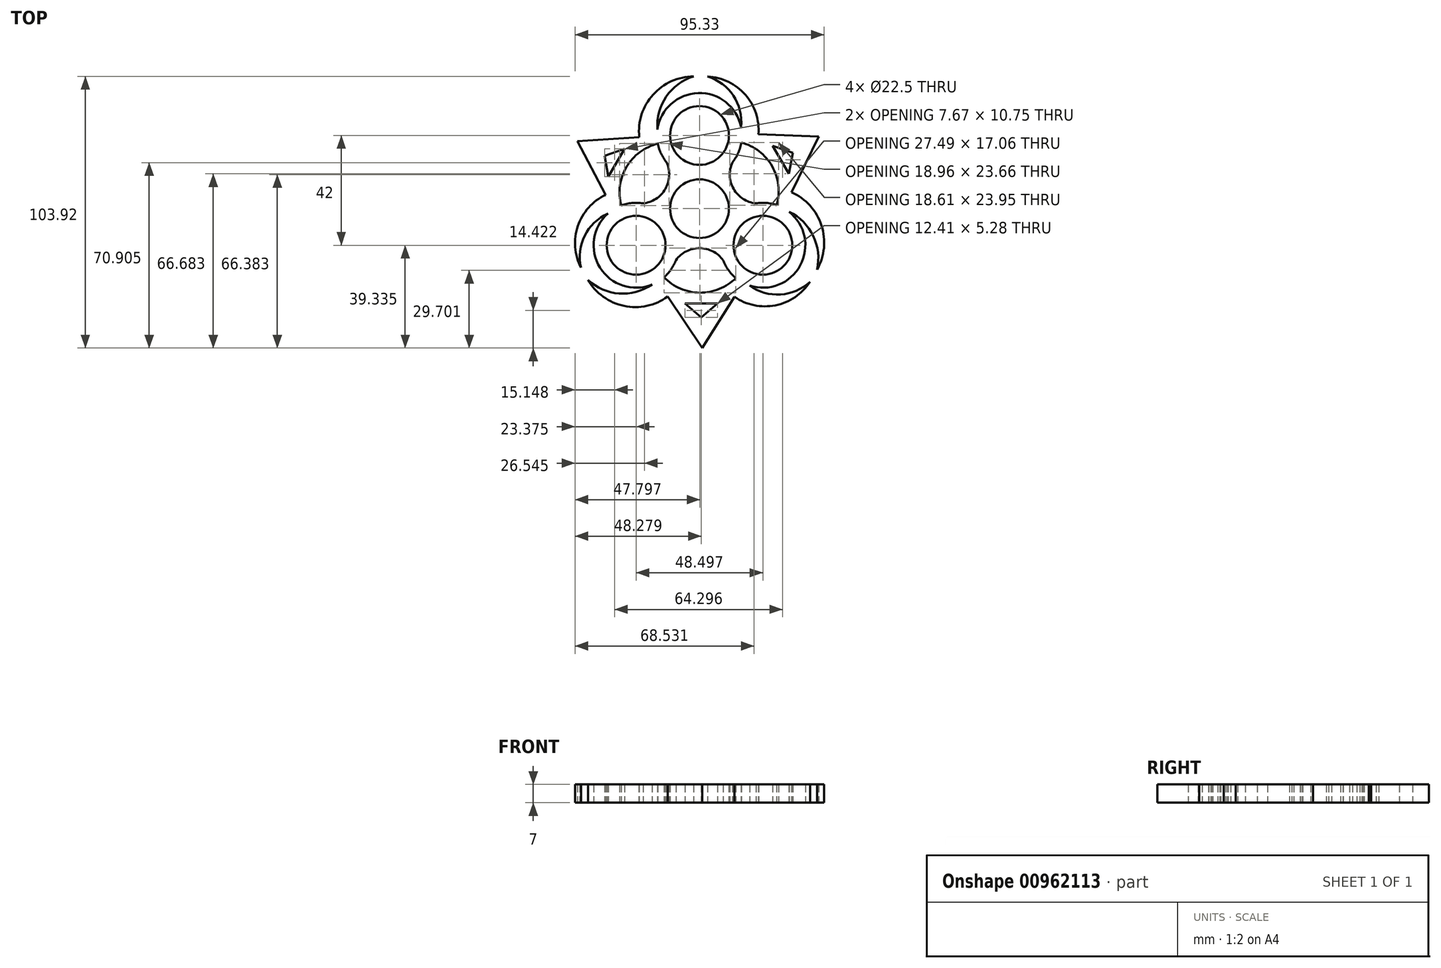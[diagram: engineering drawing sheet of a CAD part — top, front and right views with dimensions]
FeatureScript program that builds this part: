
annotation { "Feature Type Name" : "Feature", "Feature Type Description" : "" }
export const myFeature = defineFeature(function(context is Context, id is Id, definition is map)
    precondition{}
    {
        {
            var Q0;
            Q0=qCreatedBy(makeId("Top.planeOp"),FACE);
            var sketch = newSketch(context, id + "F0", { "sketchPlane" : qUnion([Q0])});
            skCircle(sketch, "E0", {"center": v(-80.13, 35.93) * mm, "radius": 11.25 * mm});
            skCircle(sketch, "E1", {"center": v(-80.13, 63.93) * mm, "radius": 11.25 * mm});
            skCircle(sketch, "E2.1.0", {"center": v(-104.38, 21.93) * mm, "radius": 11.25 * mm});
            skCircle(sketch, "E2.2.0", {"center": v(-55.88, 21.93) * mm, "radius": 11.25 * mm});
            skCircle(sketch, "E3.0", {"center": v(-80.13, 63.93) * mm, "radius": 16.25 * mm});
            skCircle(sketch, "E4.0", {"center": v(-104.38, 21.93) * mm, "radius": 16.25 * mm});
            skCircle(sketch, "E5.0", {"center": v(-55.88, 21.93) * mm, "radius": 16.25 * mm});
            skArc(sketch, "E6", {"start": v(-101.74, 37.97) * mm, "mid": v(-93.21, 43.47) * mm, "end": v(-92.68, 53.61) * mm});
            skArc(sketch, "E7.1.0", {"start": v(-71.08, 16.2) * mm, "mid": v(-80.11, 20.83) * mm, "end": v(-89.16, 16.23) * mm});
            skArc(sketch, "E7.2.0", {"start": v(-67.55, 53.64) * mm, "mid": v(-67.05, 43.5) * mm, "end": v(-58.54, 37.96) * mm});
            skLineSegment(sketch, "E8", {"start": v(-80.13, 63.93) * mm, "end": v(-80.13, 80.18) * mm});
            skLineSegment(sketch, "E9.1.0", {"start": v(-104.38, 21.93) * mm, "end": v(-118.45, 13.8) * mm});
            skLineSegment(sketch, "E9.2.0", {"start": v(-55.88, 21.93) * mm, "end": v(-41.8, 13.8) * mm});
            skArc(sketch, "E10", {"start": v(-96.07, 60.81) * mm, "mid": v(-108.04, 51.92) * mm, "end": v(-110.07, 37.15) * mm});
            skArc(sketch, "E11.1.0", {"start": v(-93.7, 9.68) * mm, "mid": v(-80.01, 3.77) * mm, "end": v(-66.2, 9.4) * mm});
            skArc(sketch, "E11.2.0", {"start": v(-50.6, 37.3) * mm, "mid": v(-52.33, 52.11) * mm, "end": v(-64.1, 61.26) * mm});
            skArc(sketch, "E12", {"start": v(-96.21, 66.22) * mm, "mid": v(-112.39, 54.09) * mm, "end": v(-115.19, 34.07) * mm});
            skArc(sketch, "E13.1.0", {"start": v(-98.31, 6.86) * mm, "mid": v(-79.72, -1.08) * mm, "end": v(-60.98, 6.5) * mm});
            skArc(sketch, "E13.2.0", {"start": v(-45.85, 34.72) * mm, "mid": v(-48.27, 54.8) * mm, "end": v(-64.21, 67.23) * mm});
            skLineSegment(sketch, "E14", {"start": v(-92.33, 2.27) * mm, "end": v(-79.1, -17.4) * mm});
            skPoint(sketch, "E14.endSnap0", {"position": v(-79.1, 2.9) * mm});
            skLineSegment(sketch, "E15", {"start": v(-79.1, -17.4) * mm, "end": v(-66.76, 2.19) * mm});
            skLineSegment(sketch, "E16.1.0", {"start": v(-34.45, 63.5) * mm, "end": v(-57.58, 64.38) * mm});
            skLineSegment(sketch, "E16.1.1", {"start": v(-44.87, 42.2) * mm, "end": v(-34.45, 63.5) * mm});
            skLineSegment(sketch, "E16.2.0", {"start": v(-126.83, 61.7) * mm, "end": v(-116.03, 41.23) * mm});
            skLineSegment(sketch, "E16.2.1", {"start": v(-103.18, 63.33) * mm, "end": v(-126.83, 61.7) * mm});
            skLineSegment(sketch, "E17", {"start": v(-85.68, -0.34) * mm, "end": v(-73.27, -0.34) * mm});
            skLineSegment(sketch, "E18", {"start": v(-73.27, -0.34) * mm, "end": v(-79.47, -5.62) * mm});
            skPoint(sketch, "E18.endSnap0", {"position": v(-79.47, -0.34) * mm});
            skLineSegment(sketch, "E19", {"start": v(-79.47, -5.62) * mm, "end": v(-85.68, -0.34) * mm});
            skPoint(sketch, "E20.center", {"position": v(3.03, 6.5) * mm});
            skLineSegment(sketch, "E21.1.0", {"start": v(-52.14, 60.01) * mm, "end": v(-44.47, 57.28) * mm});
            skLineSegment(sketch, "E21.1.1", {"start": v(-44.47, 57.28) * mm, "end": v(-45.94, 49.27) * mm});
            skLineSegment(sketch, "E21.1.2", {"start": v(-45.94, 49.27) * mm, "end": v(-52.14, 60.01) * mm});
            skLineSegment(sketch, "E21.2.0", {"start": v(-114.97, 48.13) * mm, "end": v(-116.44, 56.14) * mm});
            skLineSegment(sketch, "E21.2.1", {"start": v(-116.44, 56.14) * mm, "end": v(-108.77, 58.88) * mm});
            skLineSegment(sketch, "E21.2.2", {"start": v(-108.77, 58.88) * mm, "end": v(-114.97, 48.13) * mm});
            skArc(sketch, "E22", {"start": v(-82.36, 86.52) * mm, "mid": v(-97.92, 79.55) * mm, "end": v(-103.18, 63.33) * mm});
            skArc(sketch, "E23", {"start": v(-82.36, 86.52) * mm, "mid": v(-92.87, 78.81) * mm, "end": v(-96.21, 66.22) * mm});
            skArc(sketch, "E24", {"start": v(-57.58, 64.38) * mm, "mid": v(-62.61, 79.57) * mm, "end": v(-77.02, 86.52) * mm});
            skArc(sketch, "E25", {"start": v(-64.21, 67.23) * mm, "mid": v(-67.17, 79.17) * mm, "end": v(-77.02, 86.52) * mm});
            skArc(sketch, "E26.1.0", {"start": v(-122.82, 8.7) * mm, "mid": v(-110.9, 3.46) * mm, "end": v(-98.31, 6.86) * mm});
            skArc(sketch, "E26.1.1", {"start": v(-122.82, 8.7) * mm, "mid": v(-109, -1.28) * mm, "end": v(-92.33, 2.27) * mm});
            skArc(sketch, "E26.1.2", {"start": v(-115.19, 34.07) * mm, "mid": v(-124.05, 25.54) * mm, "end": v(-125.5, 13.33) * mm});
            skArc(sketch, "E26.1.3", {"start": v(-116.03, 41.23) * mm, "mid": v(-126.67, 29.29) * mm, "end": v(-125.5, 13.33) * mm});
            skArc(sketch, "E26.2.0", {"start": v(-35.2, 12.58) * mm, "mid": v(-36.62, 25.53) * mm, "end": v(-45.85, 34.72) * mm});
            skArc(sketch, "E26.2.1", {"start": v(-35.2, 12.58) * mm, "mid": v(-33.46, 29.54) * mm, "end": v(-44.87, 42.2) * mm});
            skArc(sketch, "E26.2.2", {"start": v(-60.98, 6.5) * mm, "mid": v(-49.17, 3.1) * mm, "end": v(-37.87, 7.95) * mm});
            skArc(sketch, "E26.2.3", {"start": v(-66.76, 2.19) * mm, "mid": v(-51.1, -1.05) * mm, "end": v(-37.87, 7.95) * mm});
            skSolve(sketch);
        }
        {
            var Q0;
            Q0=makeQuery(id+"F0.imprint","IMPRINT",FACE,{"disambiguationData":[TD([[makeQuery(id+"F0.imprint","IMPRINT",EDGE,{"derivedFrom":sQuery(id+"F0.wireOp",EDGE,"E2.1.0")}),-1.0]])]});
            var Q1;
            Q1=makeQuery(id+"F0.imprint","IMPRINT",FACE,{"disambiguationData":[TD([[makeQuery(id+"F0.imprint","IMPRINT",EDGE,{"derivedFrom":sQuery(id+"F0.wireOp",EDGE,"E0")}),-1.0]])]});
            var Q2;
            Q2=makeQuery(id+"F0.imprint","IMPRINT",FACE,{"disambiguationData":[TD([[makeQuery(id+"F0.imprint","IMPRINT",EDGE,{"derivedFrom":sQuery(id+"F0.wireOp",EDGE,"E2.2.0")}),-1.0]])]});
            var Q3;
            Q3=makeQuery(id+"F0.imprint","IMPRINT",FACE,{"disambiguationData":[TD([[makeQuery(id+"F0.imprint","IMPRINT",EDGE,{"derivedFrom":sQuery(id+"F0.wireOp",EDGE,"E1")}),-1.0]])]});
            var Q4;
            {var subQ0=sQuery(id+"F0.wireOp",EDGE,"E10");Q4=makeQuery(id+"F0.imprint","IMPRINT",FACE,{"disambiguationData":[TD([[makeQuery(id+"F0.imprint","IMPRINT",EDGE,{"derivedFrom":subQ0}),-1.0]])]});}
            var Q5;
            {var subQ0=sQuery(id+"F0.wireOp",EDGE,"E11.1.0");Q5=makeQuery(id+"F0.imprint","IMPRINT",FACE,{"disambiguationData":[TD([[makeQuery(id+"F0.imprint","IMPRINT",EDGE,{"derivedFrom":subQ0}),-1.0]])]});}
            var Q6;
            {var subQ0=sQuery(id+"F0.wireOp",EDGE,"E11.2.0");Q6=makeQuery(id+"F0.imprint","IMPRINT",FACE,{"disambiguationData":[TD([[makeQuery(id+"F0.imprint","IMPRINT",EDGE,{"derivedFrom":subQ0}),-1.0]])]});}
            var Q7;
            {var subQ0=sQuery(id+"F0.wireOp",EDGE,"GYt49fZe-YqtV-DD4k-L4cx-fm81LzEZaTT6");Q7=makeQuery(id+"F0.imprint","IMPRINT",FACE,{"disambiguationData":[TD([[makeQuery(id+"F0.imprint","IMPRINT",EDGE,{"derivedFrom":subQ0}),-1.0]])]});}
            var Q8;
            {var subQ0=sQuery(id+"F0.wireOp",EDGE,"E16.2.0");Q8=makeQuery(id+"F0.imprint","IMPRINT",FACE,{"disambiguationData":[TD([[makeQuery(id+"F0.imprint","IMPRINT",EDGE,{"derivedFrom":subQ0}),1.0]])]});}
            var Q9;
            {var subQ0=sQuery(id+"F0.wireOp",EDGE,"E14");Q9=makeQuery(id+"F0.imprint","IMPRINT",FACE,{"disambiguationData":[TD([[makeQuery(id+"F0.imprint","IMPRINT",EDGE,{"derivedFrom":subQ0}),1.0]])]});}
            var Q10;
            {var subQ0=sQuery(id+"F0.wireOp",EDGE,"E16.1.0");Q10=makeQuery(id+"F0.imprint","IMPRINT",FACE,{"disambiguationData":[TD([[makeQuery(id+"F0.imprint","IMPRINT",EDGE,{"derivedFrom":subQ0}),1.0]])]});}
            var Q11;
            {var subQ2=sQuery(id+"F0.wireOp",EDGE,"E22");Q11=makeQuery(id+"F0.imprint","IMPRINT",FACE,{"disambiguationData":[TD([[makeQuery(id+"F0.imprint","IMPRINT",EDGE,{"derivedFrom":subQ2}),1.0]])]});}
            var Q12;
            {var subQ0=sQuery(id+"F0.wireOp",EDGE,"E24");Q12=makeQuery(id+"F0.imprint","IMPRINT",FACE,{"disambiguationData":[TD([[makeQuery(id+"F0.imprint","IMPRINT",EDGE,{"derivedFrom":subQ0}),1.0]])]});}
            var Q13;
            {var subQ0=sQuery(id+"F0.wireOp",EDGE,"E26.1.2");Q13=makeQuery(id+"F0.imprint","IMPRINT",FACE,{"disambiguationData":[TD([[makeQuery(id+"F0.imprint","IMPRINT",EDGE,{"derivedFrom":subQ0}),-1.0]])]});}
            var Q14;
            {var subQ0=sQuery(id+"F0.wireOp",EDGE,"E26.1.0");Q14=makeQuery(id+"F0.imprint","IMPRINT",FACE,{"disambiguationData":[TD([[makeQuery(id+"F0.imprint","IMPRINT",EDGE,{"derivedFrom":subQ0}),-1.0]])]});}
            var Q15;
            {var subQ0=sQuery(id+"F0.wireOp",EDGE,"E26.2.2");Q15=makeQuery(id+"F0.imprint","IMPRINT",FACE,{"disambiguationData":[TD([[makeQuery(id+"F0.imprint","IMPRINT",EDGE,{"derivedFrom":subQ0}),-1.0]])]});}
            var Q16;
            {var subQ2=sQuery(id+"F0.wireOp",EDGE,"E26.2.0");Q16=makeQuery(id+"F0.imprint","IMPRINT",FACE,{"disambiguationData":[TD([[makeQuery(id+"F0.imprint","IMPRINT",EDGE,{"derivedFrom":subQ2}),-1.0]])]});}
            extrude(context, id + "F1", {"entities" : qUnion([Q0, Q1, Q2, Q3, Q4, Q5, Q6, Q7, Q8, Q9, Q10, Q11, Q12, Q13, Q14, Q15, Q16]), "depth" : 7 * mm, "offsetDistance" : 25 * mm});
        }
    });
